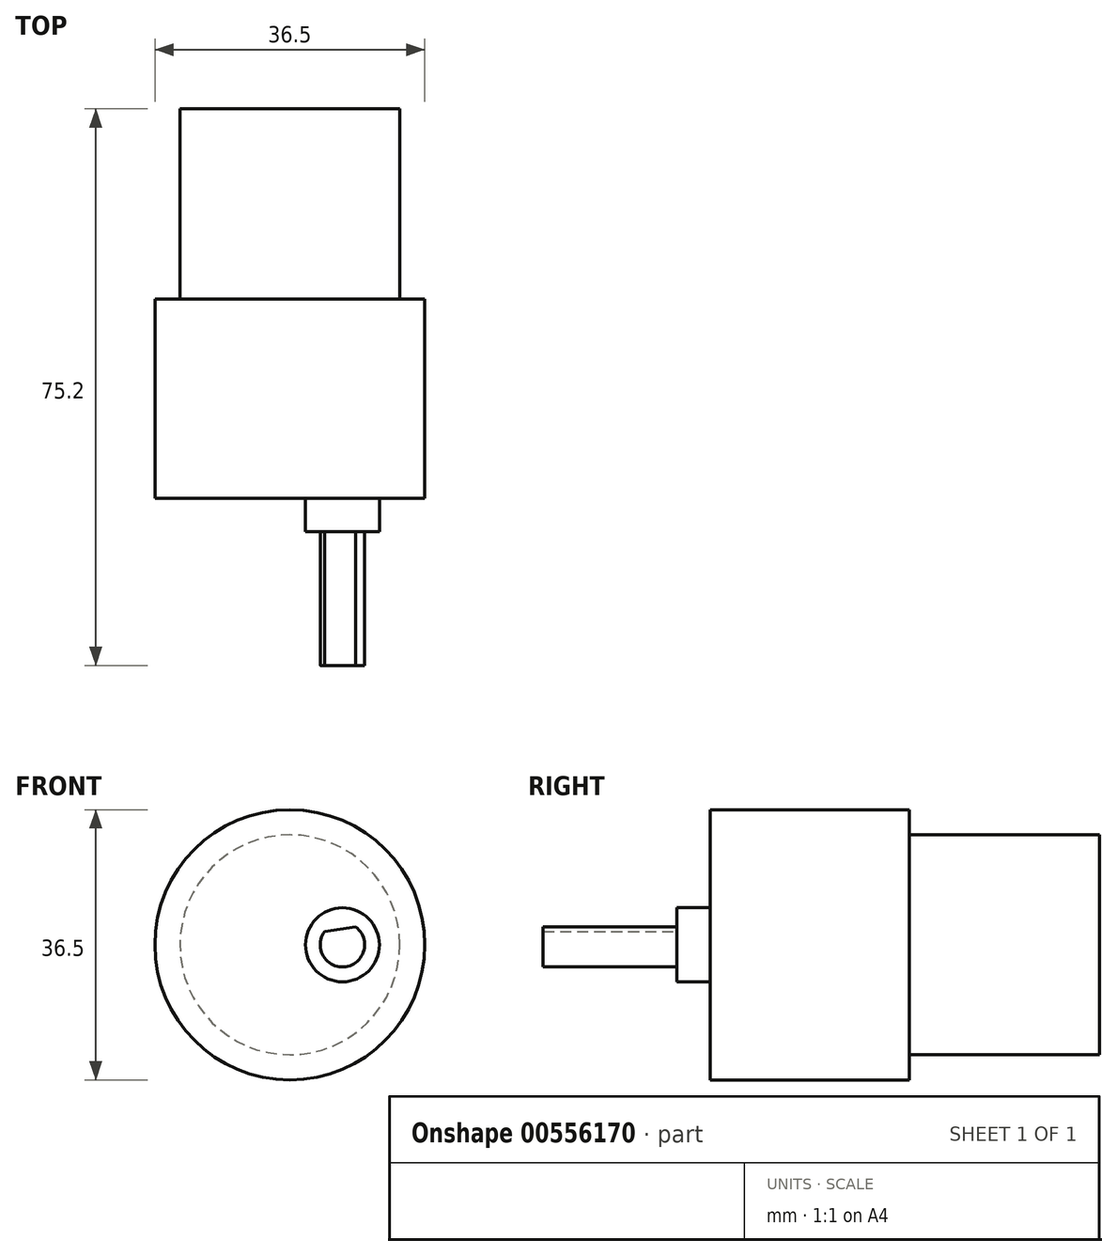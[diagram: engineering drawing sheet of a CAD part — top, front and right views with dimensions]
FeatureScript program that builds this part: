
annotation { "Feature Type Name" : "Feature", "Feature Type Description" : "" }
export const myFeature = defineFeature(function(context is Context, id is Id, definition is map)
    precondition{}
    {
        {
            var Q0;
            Q0=qCreatedBy(makeId("Front.planeOp"),FACE);
            var sketch = newSketch(context, id + "F0", { "sketchPlane" : qUnion([Q0])});
            skCircle(sketch, "E0", {"center": v(0, 0) * mm, "radius": 18.25 * mm});
            skSolve(sketch);
        }
        {
            var Q0;
            Q0=makeQuery(id+"F0.imprint","IMPRINT",FACE,{"disambiguationData":[TD([[makeQuery(id+"F0.imprint","IMPRINT",EDGE,{"derivedFrom":sQuery(id+"F0.wireOp",EDGE,"E0")}),1.0]])]});
            extrude(context, id + "F1", {"entities" : qUnion([Q0]), "depth" : 26.9 * mm, "offsetDistance" : 25.4 * mm});
        }
        {
            var Q0;
            Q0=makeQuery(id+"F1.opExtrude","CAP_FACE",FACE,{"disambiguationData":[OSD([sQuery(id+"F0.wireOp",EDGE,"E0")])],"isStart":false});
            var sketch = newSketch(context, id + "F2", { "sketchPlane" : qUnion([Q0])});
            skCircle(sketch, "E1", {"center": v(0, 15.5) * mm, "radius": 0.35 * mm});
            skLineSegment(sketch, "E2", {"start": v(-27.97, 0) * mm, "end": v(25.9, 0) * mm});
            skCircle(sketch, "E3.MirrorC", {"center": v(0, -15.5) * mm, "radius": 0.35 * mm});
            skSolve(sketch);
        }
        {
            var Q0;
            Q0=makeQuery(id+"F2.imprint","IMPRINT",FACE,{"disambiguationData":[TD([[makeQuery(id+"F2.imprint","IMPRINT",EDGE,{"derivedFrom":sQuery(id+"F2.wireOp",EDGE,"E1")}),-1.0]])]});
            var sketch = newSketch(context, id + "F3", { "sketchPlane" : qUnion([Q0])});
            skLineSegment(sketch, "E4", {"start": v(0, 18.04) * mm, "end": v(0, -17.38) * mm});
            skCircle(sketch, "E5", {"center": v(7.12, 0) * mm, "radius": 3 * mm});
            skCircle(sketch, "E6", {"center": v(7.12, 0) * mm, "radius": 5 * mm});
            skSolve(sketch);
        }
        {
            var Q0;
            {var subQ0=sQuery(id+"F3.wireOp",EDGE,"E5");var subQ1=sQuery(id+"F2.wireOp",EDGE,"E2");var subQ2=makeQuery(id+"F1.opExtrude","CAP_EDGE",EDGE,{"disambiguationData":[OSD([sQuery(id+"F0.wireOp",EDGE,"E0")])],"isStart":false});var subQ3=makeQuery(id+"F2.imprint","IMPRINT",EDGE,{"disambiguationData":[TD([[makeQuery(id+"F2.imprint","INTERSECT",VERTEX,{"disambiguationData":[OD(0.0)],"derivedFrom":[subQ2,subQ1]}),-1.0]])],"derivedFrom":subQ1});var subQ4=makeQuery(id+"F3.imprint","INTERSECT",VERTEX,{"disambiguationData":[OD(0.0)],"derivedFrom":[subQ3,subQ0]});Q0=makeQuery(id+"F3.imprint","IMPRINT",FACE,{"disambiguationData":[TD([[makeQuery(id+"F3.imprint","IMPRINT",EDGE,{"disambiguationData":[TD([[subQ4,-1.0]])],"derivedFrom":subQ0}),1.0]])]});}
            var Q1;
            {var subQ0=sQuery(id+"F3.wireOp",EDGE,"E5");var subQ1=sQuery(id+"F2.wireOp",EDGE,"E2");var subQ2=makeQuery(id+"F1.opExtrude","CAP_EDGE",EDGE,{"disambiguationData":[OSD([sQuery(id+"F0.wireOp",EDGE,"E0")])],"isStart":false});var subQ3=makeQuery(id+"F2.imprint","IMPRINT",EDGE,{"disambiguationData":[TD([[makeQuery(id+"F2.imprint","INTERSECT",VERTEX,{"disambiguationData":[OD(0.0)],"derivedFrom":[subQ2,subQ1]}),-1.0]])],"derivedFrom":subQ1});var subQ4=makeQuery(id+"F3.imprint","INTERSECT",VERTEX,{"disambiguationData":[OD(0.0)],"derivedFrom":[subQ3,subQ0]});Q1=makeQuery(id+"F3.imprint","IMPRINT",FACE,{"disambiguationData":[TD([[makeQuery(id+"F3.imprint","IMPRINT",EDGE,{"disambiguationData":[TD([[subQ4,1.0]])],"derivedFrom":subQ0}),1.0]])]});}
            var Q2;
            {var subQ0=sQuery(id+"F3.wireOp",EDGE,"E5");var subQ1=sQuery(id+"F2.wireOp",EDGE,"E2");var subQ2=makeQuery(id+"F1.opExtrude","CAP_EDGE",EDGE,{"disambiguationData":[OSD([sQuery(id+"F0.wireOp",EDGE,"E0")])],"isStart":false});var subQ3=makeQuery(id+"F2.imprint","IMPRINT",EDGE,{"disambiguationData":[TD([[makeQuery(id+"F2.imprint","INTERSECT",VERTEX,{"disambiguationData":[OD(0.0)],"derivedFrom":[subQ2,subQ1]}),-1.0]])],"derivedFrom":subQ1});var subQ4=makeQuery(id+"F3.imprint","INTERSECT",VERTEX,{"disambiguationData":[OD(0.0)],"derivedFrom":[subQ3,subQ0]});Q2=makeQuery(id+"F3.imprint","IMPRINT",FACE,{"disambiguationData":[TD([[makeQuery(id+"F3.imprint","IMPRINT",EDGE,{"disambiguationData":[TD([[subQ4,1.0]])],"derivedFrom":subQ0}),-1.0]])]});}
            var Q3;
            {var subQ0=sQuery(id+"F3.wireOp",EDGE,"E5");var subQ1=sQuery(id+"F2.wireOp",EDGE,"E2");var subQ2=makeQuery(id+"F1.opExtrude","CAP_EDGE",EDGE,{"disambiguationData":[OSD([sQuery(id+"F0.wireOp",EDGE,"E0")])],"isStart":false});var subQ3=makeQuery(id+"F2.imprint","IMPRINT",EDGE,{"disambiguationData":[TD([[makeQuery(id+"F2.imprint","INTERSECT",VERTEX,{"disambiguationData":[OD(0.0)],"derivedFrom":[subQ2,subQ1]}),-1.0]])],"derivedFrom":subQ1});var subQ4=makeQuery(id+"F3.imprint","INTERSECT",VERTEX,{"disambiguationData":[OD(0.0)],"derivedFrom":[subQ3,subQ0]});Q3=makeQuery(id+"F3.imprint","IMPRINT",FACE,{"disambiguationData":[TD([[makeQuery(id+"F3.imprint","IMPRINT",EDGE,{"disambiguationData":[TD([[subQ4,-1.0]])],"derivedFrom":subQ0}),-1.0]])]});}
            extrude(context, id + "F4", {"entities" : qUnion([Q0, Q1, Q2, Q3]), "operationType" : NewBodyOperationType.ADD, "depth" : 4.5 * mm, "offsetDistance" : 25.4 * mm});
        }
        {
            var Q0;
            Q0=makeQuery(id+"F4.opExtrude","CAP_FACE",FACE,{"disambiguationData":[OSD([sQuery(id+"F3.wireOp",EDGE,"E6")])],"isStart":false});
            var sketch = newSketch(context, id + "F5", { "sketchPlane" : qUnion([Q0])});
            skCircle(sketch, "E7", {"center": v(7.12, 0) * mm, "radius": 3 * mm});
            skLineSegment(sketch, "E8", {"start": v(7.12, 0) * mm, "end": v(8.91, 2.4) * mm});
            skLineSegment(sketch, "E9", {"start": v(7.12, 0) * mm, "end": v(4.71, 1.8) * mm});
            skLineSegment(sketch, "E10", {"start": v(4.71, 1.8) * mm, "end": v(8.91, 2.4) * mm});
            skSolve(sketch);
        }
        {
            var Q0;
            Q0=makeQuery(id+"F5.imprint","IMPRINT",FACE,{"disambiguationData":[TD([[makeQuery(id+"F5.imprint","IMPRINT",EDGE,{"derivedFrom":sQuery(id+"F5.wireOp",EDGE,"E8")}),1.0]])]});
            var Q1;
            {var subQ1=sQuery(id+"F5.wireOp",EDGE,"E8");Q1=makeQuery(id+"F5.imprint","IMPRINT",FACE,{"disambiguationData":[TD([[makeQuery(id+"F5.imprint","IMPRINT",EDGE,{"derivedFrom":subQ1}),-1.0]])]});}
            extrude(context, id + "F6", {"entities" : qUnion([Q0, Q1]), "operationType" : NewBodyOperationType.ADD, "depth" : 18.1 * mm, "offsetDistance" : 25.4 * mm});
        }
        {
            var Q0;
            Q0=makeQuery(id+"F1.opExtrude","CAP_FACE",FACE,{"disambiguationData":[OSD([sQuery(id+"F0.wireOp",EDGE,"E0")])],"isStart":true});
            var sketch = newSketch(context, id + "F7", { "sketchPlane" : qUnion([Q0])});
            skCircle(sketch, "E11", {"center": v(0, 0) * mm, "radius": 14.85 * mm});
            skSolve(sketch);
        }
        {
            var Q0;
            Q0=makeQuery(id+"F7.imprint","IMPRINT",FACE,{"disambiguationData":[TD([[makeQuery(id+"F7.imprint","IMPRINT",EDGE,{"derivedFrom":sQuery(id+"F7.wireOp",EDGE,"E11")}),1.0]])]});
            extrude(context, id + "F8", {"entities" : qUnion([Q0]), "operationType" : NewBodyOperationType.ADD, "depth" : 25.7 * mm, "offsetDistance" : 25.4 * mm});
        }
    });
